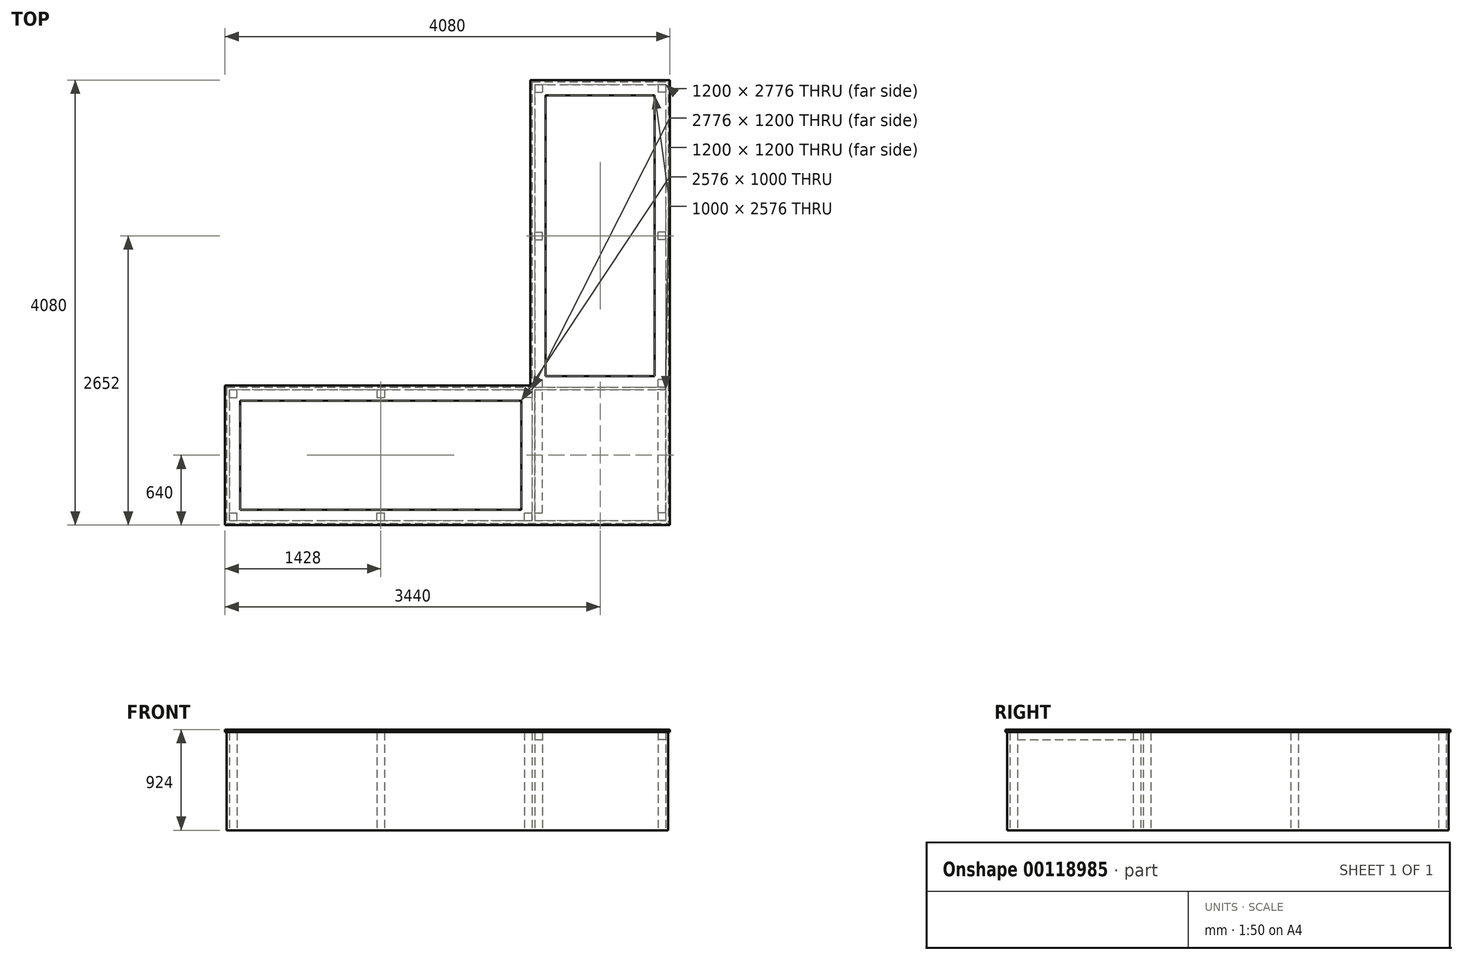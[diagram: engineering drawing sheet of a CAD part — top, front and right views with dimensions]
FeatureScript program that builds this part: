
annotation { "Feature Type Name" : "Feature", "Feature Type Description" : "" }
export const myFeature = defineFeature(function(context is Context, id is Id, definition is map)
    precondition{}
    {
        {
            var Q0;
            Q0=qCreatedBy(makeId("Top.planeOp"),FACE);
            var sketch = newSketch(context, id + "F0", { "sketchPlane" : qUnion([Q0])});
            skLineSegment(sketch, "E0", {"start": v(0, 0) * mm, "end": v(0, 4000) * mm});
            skLineSegment(sketch, "E1", {"start": v(0, 4000) * mm, "end": v(-1200, 4000) * mm});
            skLineSegment(sketch, "E2", {"start": v(-1200, 4000) * mm, "end": v(-1200, 1200) * mm});
            skLineSegment(sketch, "E3", {"start": v(-1200, 1200) * mm, "end": v(-4000, 1200) * mm});
            skLineSegment(sketch, "E4", {"start": v(-4000, 1200) * mm, "end": v(-4000, 0) * mm});
            skLineSegment(sketch, "E5", {"start": v(-4000, 0) * mm, "end": v(0, 0) * mm});
            skSolve(sketch);
        }
        {
            var Q0;
            Q0=qCreatedBy(makeId("Top.planeOp"),FACE);
            var sketch = newSketch(context, id + "F1", { "sketchPlane" : qUnion([Q0])});
            skLineSegment(sketch, "E6.bottom", {"start": v(-1200, 4000) * mm, "end": v(-1130, 4000) * mm});
            skLineSegment(sketch, "E6.top", {"start": v(-1200, 3930) * mm, "end": v(-1130, 3930) * mm});
            skLineSegment(sketch, "E6.left", {"start": v(-1200, 4000) * mm, "end": v(-1200, 3930) * mm});
            skLineSegment(sketch, "E6.right", {"start": v(-1130, 4000) * mm, "end": v(-1130, 3930) * mm});
            skLineSegment(sketch, "E7.bottom", {"start": v(0, 4000) * mm, "end": v(-70, 4000) * mm});
            skLineSegment(sketch, "E7.top", {"start": v(0, 3930) * mm, "end": v(-70, 3930) * mm});
            skLineSegment(sketch, "E7.left", {"start": v(0, 4000) * mm, "end": v(0, 3930) * mm});
            skLineSegment(sketch, "E7.right", {"start": v(-70, 4000) * mm, "end": v(-70, 3930) * mm});
            skLineSegment(sketch, "E8.bottom", {"start": v(-1200, 1224) * mm, "end": v(-1130, 1224) * mm});
            skLineSegment(sketch, "E8.top", {"start": v(-1200, 1294) * mm, "end": v(-1130, 1294) * mm});
            skLineSegment(sketch, "E8.left", {"start": v(-1200, 1224) * mm, "end": v(-1200, 1294) * mm});
            skLineSegment(sketch, "E8.right", {"start": v(-1130, 1224) * mm, "end": v(-1130, 1294) * mm});
            skLineSegment(sketch, "E9.bottom", {"start": v(-1224, 1200) * mm, "end": v(-1294, 1200) * mm});
            skLineSegment(sketch, "E9.top", {"start": v(-1224, 1130) * mm, "end": v(-1294, 1130) * mm});
            skLineSegment(sketch, "E9.left", {"start": v(-1224, 1200) * mm, "end": v(-1224, 1130) * mm});
            skLineSegment(sketch, "E9.right", {"start": v(-1294, 1200) * mm, "end": v(-1294, 1130) * mm});
            skLineSegment(sketch, "E10.bottom", {"start": v(0, 70) * mm, "end": v(-70, 70) * mm});
            skLineSegment(sketch, "E10.top", {"start": v(0, 0) * mm, "end": v(-70, 0) * mm});
            skLineSegment(sketch, "E10.left", {"start": v(0, 70) * mm, "end": v(0, 0) * mm});
            skLineSegment(sketch, "E10.right", {"start": v(-70, 70) * mm, "end": v(-70, 0) * mm});
            skLineSegment(sketch, "E11.bottom", {"start": v(-4000, 0) * mm, "end": v(-3930, 0) * mm});
            skLineSegment(sketch, "E11.top", {"start": v(-4000, 70) * mm, "end": v(-3930, 70) * mm});
            skLineSegment(sketch, "E11.left", {"start": v(-4000, 0) * mm, "end": v(-4000, 70) * mm});
            skLineSegment(sketch, "E11.right", {"start": v(-3930, 0) * mm, "end": v(-3930, 70) * mm});
            skLineSegment(sketch, "E12.bottom", {"start": v(-4000, 1130) * mm, "end": v(-3930, 1130) * mm});
            skLineSegment(sketch, "E12.top", {"start": v(-4000, 1200) * mm, "end": v(-3930, 1200) * mm});
            skLineSegment(sketch, "E12.left", {"start": v(-4000, 1130) * mm, "end": v(-4000, 1200) * mm});
            skLineSegment(sketch, "E12.right", {"start": v(-3930, 1130) * mm, "end": v(-3930, 1200) * mm});
            skLineSegment(sketch, "E13.bottom", {"start": v(-1200, 2577) * mm, "end": v(-1130, 2577) * mm});
            skLineSegment(sketch, "E13.top", {"start": v(-1200, 2647) * mm, "end": v(-1130, 2647) * mm});
            skLineSegment(sketch, "E13.left", {"start": v(-1200, 2577) * mm, "end": v(-1200, 2647) * mm});
            skLineSegment(sketch, "E13.right", {"start": v(-1130, 2577) * mm, "end": v(-1130, 2647) * mm});
            skLineSegment(sketch, "E14.bottom", {"start": v(0, 1224) * mm, "end": v(-70, 1224) * mm});
            skLineSegment(sketch, "E14.top", {"start": v(0, 1294) * mm, "end": v(-70, 1294) * mm});
            skLineSegment(sketch, "E14.left", {"start": v(0, 1224) * mm, "end": v(0, 1294) * mm});
            skLineSegment(sketch, "E14.right", {"start": v(-70, 1224) * mm, "end": v(-70, 1294) * mm});
            skLineSegment(sketch, "E15.bottom", {"start": v(0, 2577) * mm, "end": v(-70, 2577) * mm});
            skLineSegment(sketch, "E15.top", {"start": v(0, 2647) * mm, "end": v(-70, 2647) * mm});
            skLineSegment(sketch, "E15.left", {"start": v(0, 2577) * mm, "end": v(0, 2647) * mm});
            skLineSegment(sketch, "E15.right", {"start": v(-70, 2577) * mm, "end": v(-70, 2647) * mm});
            skLineSegment(sketch, "E16.bottom", {"start": v(-2647, 1200) * mm, "end": v(-2577, 1200) * mm});
            skLineSegment(sketch, "E16.top", {"start": v(-2647, 1130) * mm, "end": v(-2577, 1130) * mm});
            skLineSegment(sketch, "E16.left", {"start": v(-2647, 1200) * mm, "end": v(-2647, 1130) * mm});
            skLineSegment(sketch, "E16.right", {"start": v(-2577, 1200) * mm, "end": v(-2577, 1130) * mm});
            skLineSegment(sketch, "E17.bottom", {"start": v(-2647, 0) * mm, "end": v(-2577, 0) * mm});
            skLineSegment(sketch, "E17.top", {"start": v(-2647, 70) * mm, "end": v(-2577, 70) * mm});
            skLineSegment(sketch, "E17.left", {"start": v(-2647, 0) * mm, "end": v(-2647, 70) * mm});
            skLineSegment(sketch, "E17.right", {"start": v(-2577, 0) * mm, "end": v(-2577, 70) * mm});
            skLineSegment(sketch, "E18.bottom", {"start": v(-1294, 0) * mm, "end": v(-1224, 0) * mm});
            skLineSegment(sketch, "E18.top", {"start": v(-1294, 70) * mm, "end": v(-1224, 70) * mm});
            skLineSegment(sketch, "E18.left", {"start": v(-1294, 0) * mm, "end": v(-1294, 70) * mm});
            skLineSegment(sketch, "E18.right", {"start": v(-1224, 0) * mm, "end": v(-1224, 70) * mm});
            skLineSegment(sketch, "E19", {"start": v(-1130, 1294) * mm, "end": v(-1130, 2577) * mm, "construction": true});
            skLineSegment(sketch, "E20", {"start": v(-1130, 2647) * mm, "end": v(-1130, 3930) * mm, "construction": true});
            skLineSegment(sketch, "E21", {"start": v(-3930, 1130) * mm, "end": v(-2647, 1130) * mm, "construction": true});
            skLineSegment(sketch, "E22", {"start": v(-2577, 1130) * mm, "end": v(-1294, 1130) * mm, "construction": true});
            skLineSegment(sketch, "E23.bottom", {"start": v(-4000, 1200) * mm, "end": v(0, 1200) * mm, "construction": true});
            skLineSegment(sketch, "E23.top", {"start": v(-4000, 1224) * mm, "end": v(0, 1224) * mm, "construction": true});
            skLineSegment(sketch, "E23.left", {"start": v(-4000, 1200) * mm, "end": v(-4000, 1224) * mm, "construction": true});
            skLineSegment(sketch, "E23.right", {"start": v(0, 1200) * mm, "end": v(0, 1224) * mm, "construction": true});
            skLineSegment(sketch, "E24.bottom", {"start": v(-1200, 4000) * mm, "end": v(-1224, 4000) * mm, "construction": true});
            skLineSegment(sketch, "E24.top", {"start": v(-1200, 0) * mm, "end": v(-1224, 0) * mm, "construction": true});
            skLineSegment(sketch, "E24.left", {"start": v(-1200, 4000) * mm, "end": v(-1200, 0) * mm, "construction": true});
            skLineSegment(sketch, "E24.right", {"start": v(-1224, 4000) * mm, "end": v(-1224, 0) * mm, "construction": true});
            skSolve(sketch);
        }
        {
            var Q0;
            Q0 = qSketchRegion(id + "F1", true);
            extrude(context, id + "F2", {"entities" : qUnion([Q0]), "depth" : 900 * mm});
        }
        {
            var Q0;
            Q0=qCreatedBy(makeId("Top.planeOp"),FACE);
            var sketch = newSketch(context, id + "F3", { "sketchPlane" : qUnion([Q0])});
            skLineSegment(sketch, "E25.bottom", {"start": v(-1200, 4000) * mm, "end": v(-1224, 4000) * mm});
            skLineSegment(sketch, "E25.left", {"start": v(-1200, 4000) * mm, "end": v(-1200, 1224) * mm});
            skLineSegment(sketch, "E25.right", {"start": v(-1224, 4000) * mm, "end": v(-1224, 1224) * mm});
            skLineSegment(sketch, "E26.bottom", {"start": v(-4000, 1224) * mm, "end": v(-1224, 1224) * mm});
            skLineSegment(sketch, "E26.top", {"start": v(-4000, 1200) * mm, "end": v(-1224, 1200) * mm});
            skLineSegment(sketch, "E26.left", {"start": v(-4000, 1224) * mm, "end": v(-4000, 1200) * mm});
            skLineSegment(sketch, "E27.bottom", {"start": v(-4000, 0) * mm, "end": v(-1224, 0) * mm});
            skLineSegment(sketch, "E27.top", {"start": v(-4000, -24) * mm, "end": v(0, -24) * mm});
            skLineSegment(sketch, "E27.left", {"start": v(-4000, 0) * mm, "end": v(-4000, -24) * mm});
            skLineSegment(sketch, "E27.right", {"start": v(0, 0) * mm, "end": v(0, -24) * mm});
            skLineSegment(sketch, "E28.bottom", {"start": v(0, 4000) * mm, "end": v(24, 4000) * mm});
            skLineSegment(sketch, "E28.top", {"start": v(0, -24) * mm, "end": v(24, -24) * mm});
            skLineSegment(sketch, "E28.left", {"start": v(0, 4000) * mm, "end": v(0, 1224) * mm});
            skLineSegment(sketch, "E28.right", {"start": v(24, 4000) * mm, "end": v(24, -24) * mm});
            skLineSegment(sketch, "E29.bottom", {"start": v(-4024, 1224) * mm, "end": v(-4000, 1224) * mm});
            skLineSegment(sketch, "E29.top", {"start": v(-4024, -24) * mm, "end": v(-4000, -24) * mm});
            skLineSegment(sketch, "E29.left", {"start": v(-4024, 1224) * mm, "end": v(-4024, -24) * mm});
            skLineSegment(sketch, "E29.right", {"start": v(-4000, 1224) * mm, "end": v(-4000, -24) * mm});
            skLineSegment(sketch, "E30.bottom", {"start": v(-1224, 4024) * mm, "end": v(24, 4024) * mm});
            skLineSegment(sketch, "E30.top", {"start": v(-1224, 4000) * mm, "end": v(24, 4000) * mm});
            skLineSegment(sketch, "E30.left", {"start": v(-1224, 4024) * mm, "end": v(-1224, 4000) * mm});
            skLineSegment(sketch, "E30.right", {"start": v(24, 4024) * mm, "end": v(24, 4000) * mm});
            skLineSegment(sketch, "E31.trimOffspring", {"start": v(-1200, 1224) * mm, "end": v(0, 1224) * mm});
            skLineSegment(sketch, "E32.trimOffspring", {"start": v(-1224, 1200) * mm, "end": v(-1224, 0) * mm});
            skLineSegment(sketch, "E33.trimOffspring", {"start": v(-1200, 1200) * mm, "end": v(0, 1200) * mm});
            skLineSegment(sketch, "E34.trimOffspring", {"start": v(-1200, 1200) * mm, "end": v(-1200, 0) * mm});
            skLineSegment(sketch, "E35.trimOffspring", {"start": v(0, 1200) * mm, "end": v(0, -24) * mm});
            skLineSegment(sketch, "E36.trimOffspring", {"start": v(-1200, 0) * mm, "end": v(0, 0) * mm});
            skSolve(sketch);
        }
        {
            var Q0;
            Q0 = qSketchRegion(id + "F3", true);
            extrude(context, id + "F4", {"entities" : qUnion([Q0]), "depth" : 900 * mm});
        }
        {
            var Q0;
            Q0=makeQuery(id+"F4.opExtrude","SWEPT_FACE",FACE,{"disambiguationData":[OSD([sQuery(id+"F3.wireOp",EDGE,"E33.trimOffspring")])]});
            var sketch = newSketch(context, id + "F5", { "sketchPlane" : qUnion([Q0])});
            skLineSegment(sketch, "E37.bottom", {"start": v(-1200, 900) * mm, "end": v(-1130, 900) * mm});
            skLineSegment(sketch, "E37.top", {"start": v(-1200, 830) * mm, "end": v(-1130, 830) * mm});
            skLineSegment(sketch, "E37.left", {"start": v(-1200, 900) * mm, "end": v(-1200, 830) * mm});
            skLineSegment(sketch, "E37.right", {"start": v(-1130, 900) * mm, "end": v(-1130, 830) * mm});
            skLineSegment(sketch, "E38.bottom", {"start": v(0, 900) * mm, "end": v(-70, 900) * mm});
            skLineSegment(sketch, "E38.top", {"start": v(0, 830) * mm, "end": v(-70, 830) * mm});
            skLineSegment(sketch, "E38.left", {"start": v(0, 900) * mm, "end": v(0, 830) * mm});
            skLineSegment(sketch, "E38.right", {"start": v(-70, 900) * mm, "end": v(-70, 830) * mm});
            skSolve(sketch);
        }
        {
            var Q0;
            Q0 = qSketchRegion(id + "F5", true);
            var Q1;
            Q1=makeQuery(id+"F2.opExtrude","SWEPT_FACE",FACE,{"disambiguationData":[OSD([sQuery(id+"F1.wireOp",EDGE,"E10.bottom")])]});
            extrude(context, id + "F6", {"entities" : qUnion([Q0]), "endBound" : BoundingType.UP_TO_SURFACE, "endBoundEntityFace" : qUnion([Q1]), "depth" : 25 * mm});
        }
        {
            var Q0;
            Q0=makeQuery(id+"F6.opExtrude","SWEPT_FACE",FACE,{"disambiguationData":[OSD([sQuery(id+"F5.wireOp",EDGE,"E38.bottom")])]});
            var sketch = newSketch(context, id + "F7", { "sketchPlane" : qUnion([Q0])});
            skLineSegment(sketch, "E39", {"start": v(-1240, 4040) * mm, "end": v(40, 4040) * mm});
            skLineSegment(sketch, "E40", {"start": v(40, 4040) * mm, "end": v(40, -40) * mm});
            skLineSegment(sketch, "E41", {"start": v(40, -40) * mm, "end": v(-4040, -40) * mm});
            skLineSegment(sketch, "E42", {"start": v(-4040, -40) * mm, "end": v(-4040, 1240) * mm});
            skLineSegment(sketch, "E43", {"start": v(-4040, 1240) * mm, "end": v(-1240, 1240) * mm});
            skLineSegment(sketch, "E44", {"start": v(-1240, 1240) * mm, "end": v(-1240, 4040) * mm});
            skLineSegment(sketch, "E45.bottom", {"start": v(-1100, 1324) * mm, "end": v(-100, 1324) * mm});
            skLineSegment(sketch, "E45.top", {"start": v(-1100, 3900) * mm, "end": v(-100, 3900) * mm});
            skLineSegment(sketch, "E45.left", {"start": v(-1100, 1324) * mm, "end": v(-1100, 3900) * mm});
            skLineSegment(sketch, "E45.right", {"start": v(-100, 1324) * mm, "end": v(-100, 3900) * mm});
            skLineSegment(sketch, "E46.bottom", {"start": v(-3900, 1100) * mm, "end": v(-1324, 1100) * mm});
            skLineSegment(sketch, "E46.top", {"start": v(-3900, 100) * mm, "end": v(-1324, 100) * mm});
            skLineSegment(sketch, "E46.left", {"start": v(-3900, 1100) * mm, "end": v(-3900, 100) * mm});
            skLineSegment(sketch, "E46.right", {"start": v(-1324, 1100) * mm, "end": v(-1324, 100) * mm});
            skLineSegment(sketch, "E47", {"start": v(-1100, 3900) * mm, "end": v(-1100, 4040) * mm, "construction": true});
            skLineSegment(sketch, "E48", {"start": v(-1100, 3900) * mm, "end": v(-1240, 3900) * mm, "construction": true});
            skLineSegment(sketch, "E49", {"start": v(-3900, 1100) * mm, "end": v(-3900, 1240) * mm, "construction": true});
            skLineSegment(sketch, "E50", {"start": v(-3900, 1100) * mm, "end": v(-4040, 1100) * mm, "construction": true});
            skLineSegment(sketch, "E51", {"start": v(-100, 3900) * mm, "end": v(40, 3900) * mm, "construction": true});
            skLineSegment(sketch, "E52", {"start": v(-3900, 100) * mm, "end": v(-3900, -40) * mm, "construction": true});
            skLineSegment(sketch, "E53", {"start": v(-1100, 1324) * mm, "end": v(-1200, 1324) * mm, "construction": true});
            skLineSegment(sketch, "E54", {"start": v(-1100, 1324) * mm, "end": v(-1100, 1224) * mm, "construction": true});
            skLineSegment(sketch, "E55", {"start": v(-1324, 1100) * mm, "end": v(-1324, 1200) * mm, "construction": true});
            skLineSegment(sketch, "E56", {"start": v(-1324, 1100) * mm, "end": v(-1224, 1100) * mm, "construction": true});
            skLineSegment(sketch, "E57", {"start": v(-1324, 100) * mm, "end": v(-1324, 0) * mm, "construction": true});
            skLineSegment(sketch, "E58", {"start": v(-100, 1324) * mm, "end": v(0, 1324) * mm, "construction": true});
            skLineSegment(sketch, "E59", {"start": v(-100, 3900) * mm, "end": v(-100, 4000) * mm, "construction": true});
            skLineSegment(sketch, "E60", {"start": v(-3900, 100) * mm, "end": v(-4000, 100) * mm, "construction": true});
            skSolve(sketch);
        }
        {
            var Q0;
            Q0 = qSketchRegion(id + "F7", true);
            extrude(context, id + "F8", {"entities" : qUnion([Q0]), "depth" : 24 * mm});
        }
    });
